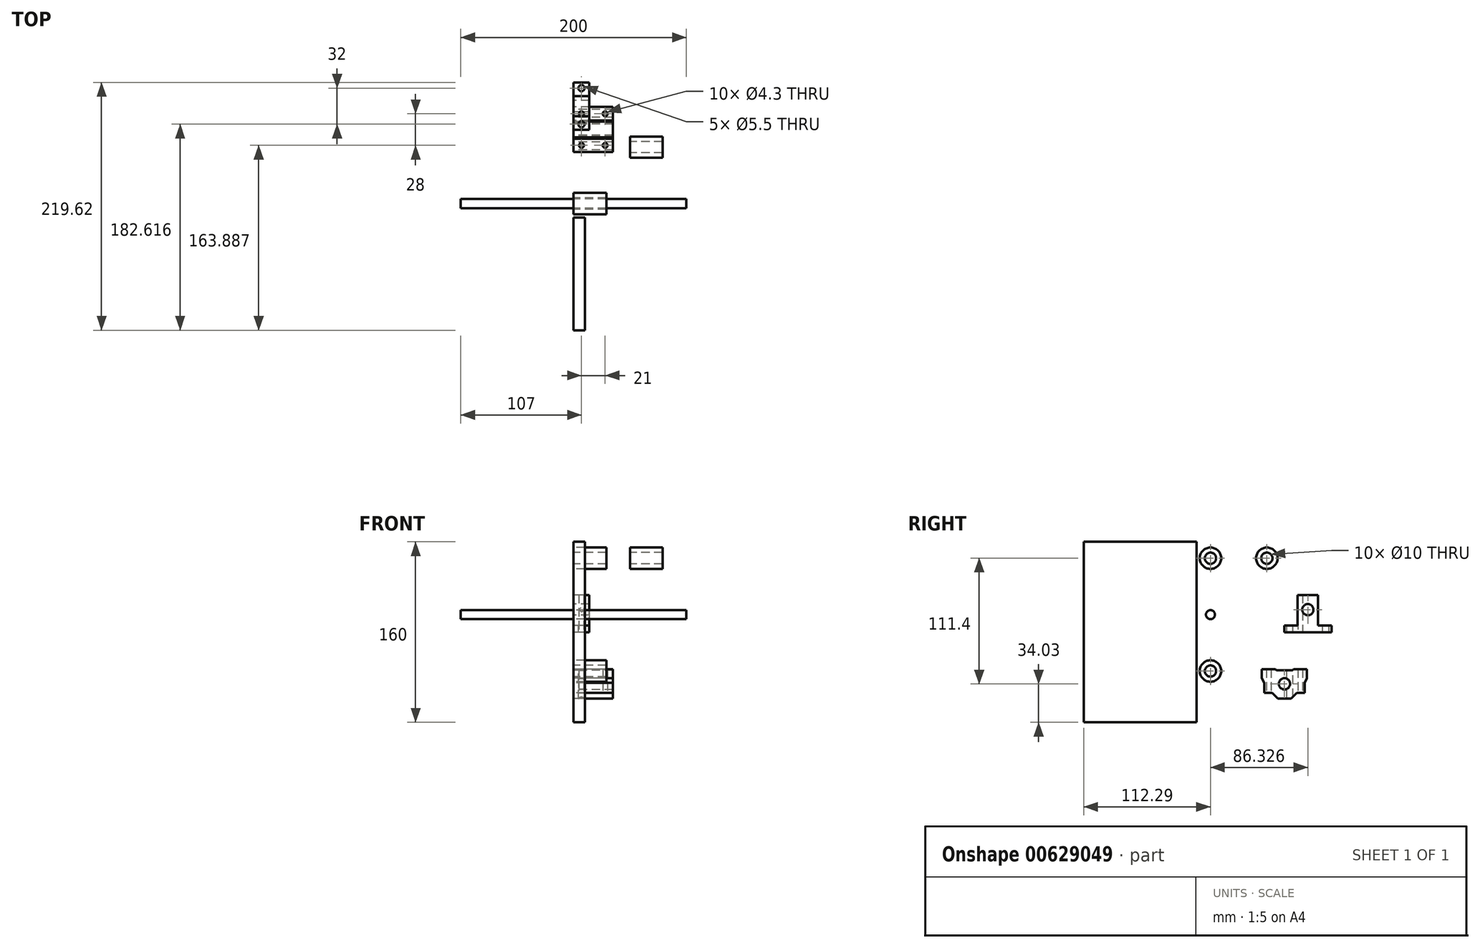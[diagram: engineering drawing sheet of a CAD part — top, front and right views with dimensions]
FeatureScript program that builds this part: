
annotation { "Feature Type Name" : "Feature", "Feature Type Description" : "" }
export const myFeature = defineFeature(function(context is Context, id is Id, definition is map)
    precondition{}
    {
        {
            var Q0;
            Q0=qCreatedBy(makeId("Right.planeOp"),FACE);
            var sketch = newSketch(context, id + "F0", { "sketchPlane" : qUnion([Q0])});
            skCircle(sketch, "E0", {"center": v(0, 50) * mm, "radius": 9.5 * mm});
            skCircle(sketch, "E1", {"center": v(0, -50) * mm, "radius": 9.5 * mm});
            skCircle(sketch, "E2", {"center": v(0, 50) * mm, "radius": 5 * mm});
            skCircle(sketch, "E3", {"center": v(0, -50) * mm, "radius": 5 * mm});
            skCircle(sketch, "E4", {"center": v(0, 0) * mm, "radius": 4 * mm});
            skLineSegment(sketch, "E5.bottom", {"start": v(-112.29, 64.57) * mm, "end": v(-12.29, 64.57) * mm});
            skLineSegment(sketch, "E5.top", {"start": v(-112.29, -95.43) * mm, "end": v(-12.29, -95.43) * mm});
            skLineSegment(sketch, "E5.left", {"start": v(-112.29, 64.57) * mm, "end": v(-112.29, -95.43) * mm});
            skLineSegment(sketch, "E5.right", {"start": v(-12.29, 64.57) * mm, "end": v(-12.29, -95.43) * mm});
            skCircle(sketch, "E6", {"center": v(86.33, 4.41) * mm, "radius": 5 * mm});
            skLineSegment(sketch, "E7.bottom", {"start": v(77.33, 17.41) * mm, "end": v(95.33, 17.41) * mm});
            skLineSegment(sketch, "E8.top", {"start": v(77.33, -9.59) * mm, "end": v(65.33, -9.59) * mm});
            skLineSegment(sketch, "E8.right", {"start": v(65.33, -15.59) * mm, "end": v(65.33, -9.59) * mm});
            skLineSegment(sketch, "E9", {"start": v(77.33, 17.41) * mm, "end": v(77.33, -9.59) * mm});
            skLineSegment(sketch, "E10", {"start": v(65.33, -15.59) * mm, "end": v(107.33, -15.59) * mm});
            skLineSegment(sketch, "E11", {"start": v(107.33, -15.59) * mm, "end": v(107.33, -9.59) * mm});
            skLineSegment(sketch, "E12", {"start": v(107.33, -9.59) * mm, "end": v(95.33, -9.59) * mm});
            skLineSegment(sketch, "E13", {"start": v(95.33, -9.59) * mm, "end": v(95.33, 17.41) * mm});
            skLineSegment(sketch, "E14", {"start": v(45.6, -48.4) * mm, "end": v(57.6, -48.4) * mm});
            skLineSegment(sketch, "E15", {"start": v(57.6, -48.4) * mm, "end": v(58.6, -49.4) * mm});
            skLineSegment(sketch, "E16", {"start": v(58.6, -49.4) * mm, "end": v(72.6, -49.4) * mm});
            skLineSegment(sketch, "E17", {"start": v(72.6, -49.4) * mm, "end": v(73.6, -48.4) * mm});
            skLineSegment(sketch, "E18", {"start": v(85.6, -48.4) * mm, "end": v(85.6, -56.4) * mm});
            skLineSegment(sketch, "E19", {"start": v(85.6, -56.4) * mm, "end": v(83.6, -60.4) * mm});
            skLineSegment(sketch, "E20", {"start": v(83.6, -60.4) * mm, "end": v(83.6, -69.4) * mm});
            skLineSegment(sketch, "E21", {"start": v(83.6, -69.4) * mm, "end": v(76.6, -69.4) * mm});
            skLineSegment(sketch, "E22", {"start": v(71.6, -74.4) * mm, "end": v(59.6, -74.4) * mm});
            skLineSegment(sketch, "E23", {"start": v(54.6, -69.4) * mm, "end": v(47.6, -69.4) * mm});
            skLineSegment(sketch, "E24", {"start": v(47.6, -69.4) * mm, "end": v(47.6, -60.4) * mm});
            skLineSegment(sketch, "E25", {"start": v(47.6, -60.4) * mm, "end": v(45.6, -56.4) * mm});
            skLineSegment(sketch, "E26", {"start": v(45.6, -56.4) * mm, "end": v(45.6, -48.4) * mm});
            skCircle(sketch, "E27", {"center": v(65.6, -61.4) * mm, "radius": 5 * mm});
            skPoint(sketch, "E27.centerSnap0", {"position": v(65.6, -74.4) * mm});
            skLineSegment(sketch, "E28", {"start": v(59.6, -74.4) * mm, "end": v(54.6, -69.4) * mm});
            skLineSegment(sketch, "E29", {"start": v(76.6, -69.4) * mm, "end": v(71.6, -74.4) * mm});
            skLineSegment(sketch, "E30", {"start": v(85.6, -48.4) * mm, "end": v(73.6, -48.4) * mm});
            skSolve(sketch);
        }
        {
            var Q0;
            Q0=makeQuery(id+"F0.imprint","IMPRINT",FACE,{"disambiguationData":[TD([[makeQuery(id+"F0.imprint","IMPRINT",EDGE,{"derivedFrom":sQuery(id+"F0.wireOp",EDGE,"E0")}),1.0]])]});
            extrude(context, id + "F1", {"entities" : qUnion([Q0]), "depth" : 29 * mm, "offsetDistance" : 25 * mm});
        }
        {
            var Q0;
            Q0=makeQuery(id+"F0.imprint","IMPRINT",FACE,{"disambiguationData":[TD([[makeQuery(id+"F0.imprint","IMPRINT",EDGE,{"derivedFrom":sQuery(id+"F0.wireOp",EDGE,"E4")}),1.0]])]});
            extrude(context, id + "F2", {"entities" : qUnion([Q0]), "endBound" : BoundingType.SYMMETRIC, "depth" : 200 * mm, "offsetDistance" : 25 * mm});
        }
        {
            var Q0;
            Q0=makeQuery(id+"F0.imprint","IMPRINT",FACE,{"disambiguationData":[TD([[makeQuery(id+"F0.imprint","IMPRINT",EDGE,{"derivedFrom":sQuery(id+"F0.wireOp",EDGE,"E1")}),1.0]])]});
            extrude(context, id + "F3", {"entities" : qUnion([Q0]), "depth" : 29 * mm, "offsetDistance" : 25 * mm});
        }
        {
            var Q0;
            Q0=makeQuery(id+"F0.imprint","IMPRINT",FACE,{"disambiguationData":[TD([[makeQuery(id+"F0.imprint","IMPRINT",EDGE,{"derivedFrom":sQuery(id+"F0.wireOp",EDGE,"E5.bottom")}),-1.0]])]});
            extrude(context, id + "F4", {"entities" : qUnion([Q0]), "depth" : 10 * mm, "offsetDistance" : 25 * mm});
        }
        {
            var Q0;
            Q0=makeQuery(id+"F0.imprint","IMPRINT",FACE,{"disambiguationData":[TD([[makeQuery(id+"F0.imprint","IMPRINT",EDGE,{"derivedFrom":sQuery(id+"F0.wireOp",EDGE,"E6")}),-1.0]])]});
            extrude(context, id + "F5", {"entities" : qUnion([Q0]), "depth" : 14 * mm, "offsetDistance" : 25 * mm});
        }
        {
            var Q0;
            Q0=makeQuery(id+"F5.opExtrude","SWEPT_FACE",FACE,{"disambiguationData":[OSD([sQuery(id+"F0.wireOp",EDGE,"E8.top")])]});
            var sketch = newSketch(context, id + "F6", { "sketchPlane" : qUnion([Q0])});
            skCircle(sketch, "E31", {"center": v(7, 70.33) * mm, "radius": 2.75 * mm});
            skPoint(sketch, "E31.centerSnap0", {"position": v(7, 65.33) * mm});
            skCircle(sketch, "E32", {"center": v(7, 102.33) * mm, "radius": 2.75 * mm});
            skSolve(sketch);
        }
        {
            var Q0;
            Q0=makeQuery(id+"F6.imprint","IMPRINT",FACE,{"disambiguationData":[TD([[makeQuery(id+"F6.imprint","IMPRINT",EDGE,{"derivedFrom":sQuery(id+"F6.wireOp",EDGE,"E32")}),1.0]])]});
            var Q1;
            Q1=makeQuery(id+"F6.imprint","IMPRINT",FACE,{"disambiguationData":[TD([[makeQuery(id+"F6.imprint","IMPRINT",EDGE,{"derivedFrom":sQuery(id+"F6.wireOp",EDGE,"E31")}),1.0]])]});
            extrude(context, id + "F7", {"entities" : qUnion([Q0, Q1]), "operationType" : NewBodyOperationType.REMOVE, "endBound" : BoundingType.THROUGH_ALL, "oppositeDirection" : true, "depth" : 25 * mm, "offsetDistance" : 25 * mm});
        }
        {
            var Q0;
            Q0=makeQuery(id+"F0.imprint","IMPRINT",FACE,{"disambiguationData":[TD([[makeQuery(id+"F0.imprint","IMPRINT",EDGE,{"derivedFrom":sQuery(id+"F0.wireOp",EDGE,"E14")}),-1.0]])]});
            extrude(context, id + "F8", {"entities" : qUnion([Q0]), "depth" : 35 * mm, "offsetDistance" : 25 * mm});
        }
        {
            var Q0;
            Q0=makeQuery(id+"F8.opExtrude","SWEPT_FACE",FACE,{"disambiguationData":[OSD([sQuery(id+"F0.wireOp",EDGE,"E21")])]});
            var sketch = newSketch(context, id + "F9", { "sketchPlane" : qUnion([Q0])});
            skCircle(sketch, "E33", {"center": v(28, -79.6) * mm, "radius": 2.15 * mm});
            skCircle(sketch, "E34", {"center": v(7, -79.6) * mm, "radius": 2.15 * mm});
            skCircle(sketch, "E35", {"center": v(28, -51.6) * mm, "radius": 2.15 * mm});
            skCircle(sketch, "E36", {"center": v(7, -51.6) * mm, "radius": 2.15 * mm});
            skSolve(sketch);
        }
        {
            var Q0;
            Q0=makeQuery(id+"F9.imprint","IMPRINT",FACE,{"disambiguationData":[TD([[makeQuery(id+"F9.imprint","IMPRINT",EDGE,{"derivedFrom":sQuery(id+"F9.wireOp",EDGE,"E35")}),1.0]])]});
            var Q1;
            Q1=makeQuery(id+"F9.imprint","IMPRINT",FACE,{"disambiguationData":[TD([[makeQuery(id+"F9.imprint","IMPRINT",EDGE,{"derivedFrom":sQuery(id+"F9.wireOp",EDGE,"E36")}),1.0]])]});
            var Q2;
            Q2=makeQuery(id+"F9.imprint","IMPRINT",FACE,{"disambiguationData":[TD([[makeQuery(id+"F9.imprint","IMPRINT",EDGE,{"derivedFrom":sQuery(id+"F9.wireOp",EDGE,"E33")}),1.0]])]});
            var Q3;
            Q3=makeQuery(id+"F9.imprint","IMPRINT",FACE,{"disambiguationData":[TD([[makeQuery(id+"F9.imprint","IMPRINT",EDGE,{"derivedFrom":sQuery(id+"F9.wireOp",EDGE,"E34")}),1.0]])]});
            extrude(context, id + "F10", {"entities" : qUnion([Q0, Q1, Q2, Q3]), "operationType" : NewBodyOperationType.REMOVE, "endBound" : BoundingType.THROUGH_ALL, "oppositeDirection" : true, "depth" : 25 * mm, "offsetDistance" : 25 * mm});
        }
        {
            var Q0;
            Q0=makeQuery(id+"F1.opExtrude","SWEPT_BODY",BODY,{"disambiguationData":[OSD([sQuery(id+"F0.wireOp",EDGE,"E0"),sQuery(id+"F0.wireOp",EDGE,"E2")])]});
            transform(context, id + "F11", {"entities" : qUnion([Q0]), "transformType" : TransformType.TRANSLATION_3D, "dx" : 50 * mm, "dy" : 50 * mm, "dz" : 0 * mm, "makeCopy" : true});
        }
    });
